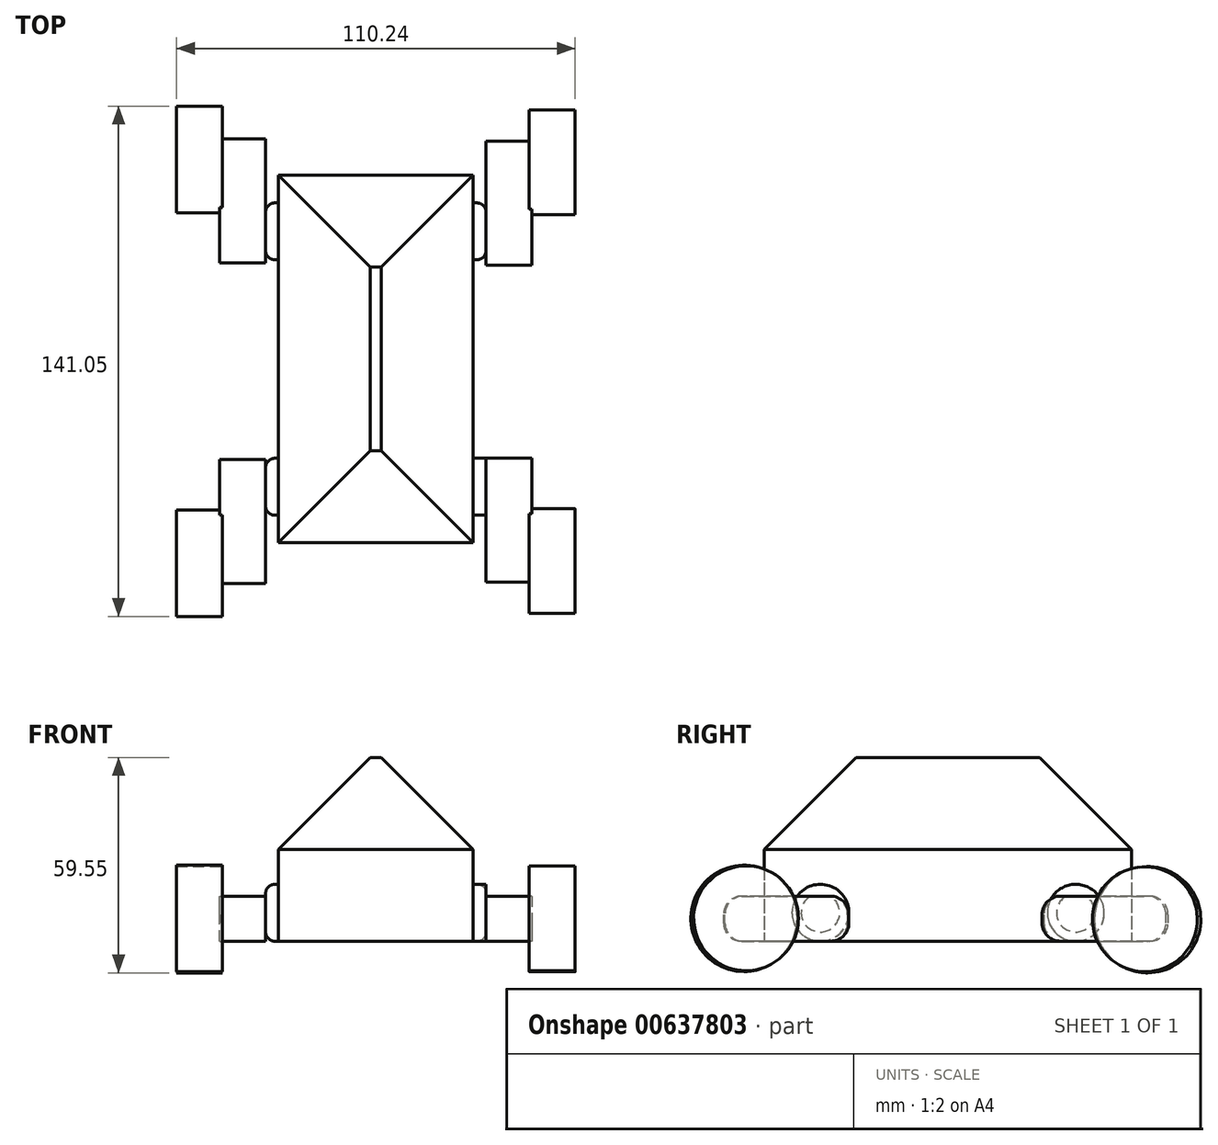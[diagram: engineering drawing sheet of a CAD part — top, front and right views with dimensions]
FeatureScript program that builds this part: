
annotation { "Feature Type Name" : "Feature", "Feature Type Description" : "" }
export const myFeature = defineFeature(function(context is Context, id is Id, definition is map)
    precondition{}
    {
        {
            var Q0;
            Q0=qCreatedBy(makeId("Top.planeOp"),FACE);
            var sketch = newSketch(context, id + "F0", { "sketchPlane" : qUnion([Q0])});
            skLineSegment(sketch, "E0.bottom", {"start": v(26.9, -50.8) * mm, "end": v(-26.9, -50.8) * mm});
            skLineSegment(sketch, "E0.top", {"start": v(26.9, 50.8) * mm, "end": v(-26.9, 50.8) * mm});
            skLineSegment(sketch, "E0.left", {"start": v(26.9, -50.8) * mm, "end": v(26.9, 50.8) * mm});
            skLineSegment(sketch, "E0.right", {"start": v(-26.9, -50.8) * mm, "end": v(-26.9, 50.8) * mm});
            skPoint(sketch, "E0.middle", {"position": v(0, 0) * mm});
            skSolve(sketch);
        }
        {
            var Q0;
            Q0=makeQuery(id+"F0.imprint","IMPRINT",FACE,{"disambiguationData":[TD([[makeQuery(id+"F0.imprint","IMPRINT",EDGE,{"derivedFrom":sQuery(id+"F0.wireOp",EDGE,"E0.bottom")}),-1.0]])]});
            extrude(context, id + "F1", {"entities" : qUnion([Q0]), "depth" : 25.4 * mm, "offsetDistance" : 25.4 * mm});
        }
        {
            var Q0;
            Q0=qCreatedBy(makeId("Right.planeOp"),FACE);
            var sketch = newSketch(context, id + "F2", { "sketchPlane" : qUnion([Q0])});
            skCircle(sketch, "E1", {"center": v(-35.31, 7.87) * mm, "radius": 7.87 * mm});
            skCircle(sketch, "E2", {"center": v(35.31, 7.87) * mm, "radius": 7.87 * mm});
            skSolve(sketch);
        }
        {
            var Q0;
            Q0 = qSketchRegion(id + "F2", true);
            extrude(context, id + "F3", {"entities" : qUnion([Q0]), "operationType" : NewBodyOperationType.ADD, "depth" : 30.48 * mm, "offsetDistance" : 25.4 * mm});
        }
        {
            var Q0;
            Q0=qCreatedBy(makeId("Right.planeOp"),FACE);
            var sketch = newSketch(context, id + "F4", { "sketchPlane" : qUnion([Q0])});
            skCircle(sketch, "E3", {"center": v(35.31, 7.87) * mm, "radius": 7.87 * mm});
            skCircle(sketch, "E4", {"center": v(-35.31, 7.87) * mm, "radius": 7.87 * mm});
            skSolve(sketch);
        }
        {
            var Q0;
            Q0 = qSketchRegion(id + "F4", true);
            extrude(context, id + "F5", {"entities" : qUnion([Q0]), "operationType" : NewBodyOperationType.ADD, "oppositeDirection" : true, "depth" : 30.48 * mm, "offsetDistance" : 25.4 * mm});
        }
        {
            var Q0;
            Q0=makeQuery(id+"F3.opExtrude","CAP_FACE",FACE,{"disambiguationData":[OSD([sQuery(id+"F2.wireOp",EDGE,"E1")])],"isStart":false});
            var Q1;
            Q1=makeQuery(id+"F3.opExtrude","CAP_FACE",FACE,{"disambiguationData":[OSD([sQuery(id+"F2.wireOp",EDGE,"E2")])],"isStart":false});
            var Q2;
            Q2=makeQuery(id+"F5.opExtrude","CAP_FACE",FACE,{"disambiguationData":[OSD([sQuery(id+"F4.wireOp",EDGE,"E3")])],"isStart":false});
            var Q3;
            Q3=makeQuery(id+"F5.opExtrude","CAP_FACE",FACE,{"disambiguationData":[OSD([sQuery(id+"F4.wireOp",EDGE,"E4")])],"isStart":false});
            fillet(context, id + "F6", {"entities" : qUnion([Q0, Q1, Q2, Q3]), "radius" : 2.54 * mm, "allowEdgeOverflow" : false});
        }
        {
            var Q0;
            Q0=qCreatedBy(makeId("Top.planeOp"),FACE);
            var sketch = newSketch(context, id + "F7", { "sketchPlane" : qUnion([Q0])});
            skLineSegment(sketch, "E5.bottom", {"start": v(-30.48, -27.81) * mm, "end": v(-43.18, -27.81) * mm});
            skLineSegment(sketch, "E5.top", {"start": v(-30.48, -62.1) * mm, "end": v(-43.18, -62.1) * mm});
            skLineSegment(sketch, "E5.left", {"start": v(-30.48, -27.81) * mm, "end": v(-30.48, -62.1) * mm});
            skLineSegment(sketch, "E5.right", {"start": v(-43.18, -27.81) * mm, "end": v(-43.18, -62.1) * mm});
            skPoint(sketch, "E5.middle", {"position": v(-36.83, -44.96) * mm});
            skLineSegment(sketch, "E6.bottom", {"start": v(-30.48, 60.82) * mm, "end": v(-43.18, 60.82) * mm});
            skLineSegment(sketch, "E6.top", {"start": v(-30.48, 26.53) * mm, "end": v(-43.18, 26.53) * mm});
            skLineSegment(sketch, "E6.left", {"start": v(-30.48, 60.82) * mm, "end": v(-30.48, 26.53) * mm});
            skLineSegment(sketch, "E6.right", {"start": v(-43.18, 60.82) * mm, "end": v(-43.18, 26.53) * mm});
            skLineSegment(sketch, "E7.bottom", {"start": v(43.18, 60.28) * mm, "end": v(30.48, 60.28) * mm});
            skLineSegment(sketch, "E7.top", {"start": v(43.18, 25.99) * mm, "end": v(30.48, 25.99) * mm});
            skLineSegment(sketch, "E7.left", {"start": v(43.18, 60.28) * mm, "end": v(43.18, 25.99) * mm});
            skLineSegment(sketch, "E7.right", {"start": v(30.48, 60.28) * mm, "end": v(30.48, 25.99) * mm});
            skLineSegment(sketch, "E8.bottom", {"start": v(43.18, -27.44) * mm, "end": v(30.48, -27.44) * mm});
            skLineSegment(sketch, "E8.top", {"start": v(43.18, -61.73) * mm, "end": v(30.48, -61.73) * mm});
            skLineSegment(sketch, "E8.left", {"start": v(43.18, -27.44) * mm, "end": v(43.18, -61.73) * mm});
            skLineSegment(sketch, "E8.right", {"start": v(30.48, -27.44) * mm, "end": v(30.48, -61.73) * mm});
            skSolve(sketch);
        }
        {
            var Q0;
            Q0=makeQuery(id+"F7.imprint","IMPRINT",FACE,{"disambiguationData":[TD([[makeQuery(id+"F7.imprint","IMPRINT",EDGE,{"derivedFrom":sQuery(id+"F7.wireOp",EDGE,"E8.bottom")}),1.0]])]});
            var Q1;
            Q1=makeQuery(id+"F7.imprint","IMPRINT",FACE,{"disambiguationData":[TD([[makeQuery(id+"F7.imprint","IMPRINT",EDGE,{"derivedFrom":sQuery(id+"F7.wireOp",EDGE,"E7.bottom")}),1.0]])]});
            var Q2;
            Q2=makeQuery(id+"F7.imprint","IMPRINT",FACE,{"disambiguationData":[TD([[makeQuery(id+"F7.imprint","IMPRINT",EDGE,{"derivedFrom":sQuery(id+"F7.wireOp",EDGE,"E6.bottom")}),1.0]])]});
            var Q3;
            Q3=makeQuery(id+"F7.imprint","IMPRINT",FACE,{"disambiguationData":[TD([[makeQuery(id+"F7.imprint","IMPRINT",EDGE,{"derivedFrom":sQuery(id+"F7.wireOp",EDGE,"E5.bottom")}),1.0]])]});
            extrude(context, id + "F8", {"entities" : qUnion([Q0, Q1, Q2, Q3]), "operationType" : NewBodyOperationType.ADD, "depth" : 12.45 * mm, "offsetDistance" : 25.4 * mm});
        }
        {
            var Q0;
            Q0=makeQuery(id+"F8.opExtrude","CAP_EDGE",EDGE,{"disambiguationData":[OSD([sQuery(id+"F7.wireOp",EDGE,"E8.top")])],"isStart":false});
            var Q1;
            Q1=makeQuery(id+"F8.opExtrude","CAP_EDGE",EDGE,{"disambiguationData":[OSD([sQuery(id+"F7.wireOp",EDGE,"E8.top")])],"isStart":true});
            var Q2;
            Q2=makeQuery(id+"F8.opExtrude","CAP_EDGE",EDGE,{"disambiguationData":[OSD([sQuery(id+"F7.wireOp",EDGE,"E8.bottom")])],"isStart":false});
            var Q3;
            Q3=makeQuery(id+"F8.opExtrude","CAP_EDGE",EDGE,{"disambiguationData":[OSD([sQuery(id+"F7.wireOp",EDGE,"E8.bottom")])],"isStart":true});
            var Q4;
            Q4=makeQuery(id+"F8.opExtrude","CAP_EDGE",EDGE,{"disambiguationData":[OSD([sQuery(id+"F7.wireOp",EDGE,"E7.bottom")])],"isStart":true});
            var Q5;
            Q5=makeQuery(id+"F8.opExtrude","CAP_EDGE",EDGE,{"disambiguationData":[OSD([sQuery(id+"F7.wireOp",EDGE,"E7.bottom")])],"isStart":false});
            var Q6;
            Q6=makeQuery(id+"F8.opExtrude","CAP_EDGE",EDGE,{"disambiguationData":[OSD([sQuery(id+"F7.wireOp",EDGE,"E7.top")])],"isStart":true});
            var Q7;
            Q7=makeQuery(id+"F8.opExtrude","CAP_EDGE",EDGE,{"disambiguationData":[OSD([sQuery(id+"F7.wireOp",EDGE,"E7.top")])],"isStart":false});
            var Q8;
            Q8=makeQuery(id+"F8.opExtrude","CAP_EDGE",EDGE,{"disambiguationData":[OSD([sQuery(id+"F7.wireOp",EDGE,"E5.top")])],"isStart":false});
            var Q9;
            Q9=makeQuery(id+"F8.opExtrude","CAP_EDGE",EDGE,{"disambiguationData":[OSD([sQuery(id+"F7.wireOp",EDGE,"E5.top")])],"isStart":true});
            var Q10;
            Q10=makeQuery(id+"F8.opExtrude","CAP_EDGE",EDGE,{"disambiguationData":[OSD([sQuery(id+"F7.wireOp",EDGE,"E5.bottom")])],"isStart":false});
            var Q11;
            Q11=makeQuery(id+"F8.opExtrude","CAP_EDGE",EDGE,{"disambiguationData":[OSD([sQuery(id+"F7.wireOp",EDGE,"E6.bottom")])],"isStart":false});
            var Q12;
            Q12=makeQuery(id+"F8.opExtrude","CAP_EDGE",EDGE,{"disambiguationData":[OSD([sQuery(id+"F7.wireOp",EDGE,"E5.bottom")])],"isStart":true});
            var Q13;
            Q13=makeQuery(id+"F8.opExtrude","CAP_EDGE",EDGE,{"disambiguationData":[OSD([sQuery(id+"F7.wireOp",EDGE,"E6.bottom")])],"isStart":true});
            var Q14;
            Q14=makeQuery(id+"F8.opExtrude","CAP_EDGE",EDGE,{"disambiguationData":[OSD([sQuery(id+"F7.wireOp",EDGE,"E6.top")])],"isStart":true});
            var Q15;
            Q15=makeQuery(id+"F8.opExtrude","CAP_EDGE",EDGE,{"disambiguationData":[OSD([sQuery(id+"F7.wireOp",EDGE,"E6.top")])],"isStart":false});
            fillet(context, id + "F9", {"entities" : qUnion([Q0, Q1, Q2, Q3, Q4, Q5, Q6, Q7, Q8, Q9, Q10, Q11, Q12, Q13, Q14, Q15]), "radius" : 5.08 * mm, "tangentPropagation" : true, "allowEdgeOverflow" : false});
        }
        {
            var Q0;
            Q0=qCreatedBy(makeId("Right.planeOp"),FACE);
            cPlane(context, id + "F10", {"entities" : qUnion([Q0]), "cplaneType" : CPlaneType.OFFSET, "offset" : 42.42 * mm, "width" : 152.4 * mm, "height" : 152.4 * mm});
        }
        {
            var Q0;
            Q0=qCreatedBy(makeId("Right.planeOp"),FACE);
            cPlane(context, id + "F11", {"entities" : qUnion([Q0]), "cplaneType" : CPlaneType.OFFSET, "offset" : 42.42 * mm, "oppositeDirection" : true, "width" : 152.4 * mm, "height" : 152.4 * mm});
        }
        {
            var Q0;
            Q0=qCreatedBy(id+"F10.planeOp",FACE);
            var sketch = newSketch(context, id + "F12", { "sketchPlane" : qUnion([Q0])});
            skCircle(sketch, "E9", {"center": v(-55.87, 6.33) * mm, "radius": 14.5 * mm});
            skCircle(sketch, "E10", {"center": v(54.43, 6.06) * mm, "radius": 14.5 * mm});
            skSolve(sketch);
        }
        {
            var Q0;
            Q0=makeQuery(id+"F12.imprint","IMPRINT",FACE,{"disambiguationData":[TD([[makeQuery(id+"F12.imprint","IMPRINT",EDGE,{"derivedFrom":sQuery(id+"F12.wireOp",EDGE,"E9")}),1.0]])]});
            var Q1;
            Q1=makeQuery(id+"F12.imprint","IMPRINT",FACE,{"disambiguationData":[TD([[makeQuery(id+"F12.imprint","IMPRINT",EDGE,{"derivedFrom":sQuery(id+"F12.wireOp",EDGE,"E10")}),1.0]])]});
            extrude(context, id + "F13", {"entities" : qUnion([Q0, Q1]), "operationType" : NewBodyOperationType.ADD, "depth" : 12.7 * mm, "offsetDistance" : 25.4 * mm});
        }
        {
            var Q0;
            Q0=qCreatedBy(id+"F11.planeOp",FACE);
            var sketch = newSketch(context, id + "F14", { "sketchPlane" : qUnion([Q0])});
            skCircle(sketch, "E11", {"center": v(55.19, 5.95) * mm, "radius": 14.7 * mm});
            skCircle(sketch, "E12", {"center": v(-56.46, 6.3) * mm, "radius": 14.7 * mm});
            skSolve(sketch);
        }
        {
            var Q0;
            Q0=makeQuery(id+"F14.imprint","IMPRINT",FACE,{"disambiguationData":[TD([[makeQuery(id+"F14.imprint","IMPRINT",EDGE,{"derivedFrom":sQuery(id+"F14.wireOp",EDGE,"E11")}),1.0]])]});
            var Q1;
            Q1=makeQuery(id+"F14.imprint","IMPRINT",FACE,{"disambiguationData":[TD([[makeQuery(id+"F14.imprint","IMPRINT",EDGE,{"derivedFrom":sQuery(id+"F14.wireOp",EDGE,"E12")}),1.0]])]});
            extrude(context, id + "F15", {"entities" : qUnion([Q0, Q1]), "operationType" : NewBodyOperationType.ADD, "oppositeDirection" : true, "depth" : 12.7 * mm, "offsetDistance" : 25.4 * mm});
        }
        {
            var Q0;
            Q0=makeQuery(id+"F1.opExtrude","CAP_FACE",FACE,{"disambiguationData":[OSD([sQuery(id+"F0.wireOp",EDGE,"E0.bottom"),sQuery(id+"F0.wireOp",EDGE,"E0.top"),sQuery(id+"F0.wireOp",EDGE,"E0.left"),sQuery(id+"F0.wireOp",EDGE,"E0.right")])],"isStart":false});
            cPlane(context, id + "F16", {"entities" : qUnion([Q0]), "cplaneType" : CPlaneType.OFFSET, "offset" : 0 * mm, "width" : 152.4 * mm, "height" : 152.4 * mm});
        }
        {
            var Q0;
            Q0=qCreatedBy(id+"F16.planeOp",FACE);
            var sketch = newSketch(context, id + "F17", { "sketchPlane" : qUnion([Q0])});
            skLineSegment(sketch, "E13.bottom", {"start": v(26.9, -50.8) * mm, "end": v(-26.9, -50.8) * mm});
            skLineSegment(sketch, "E13.top", {"start": v(26.9, 50.8) * mm, "end": v(-26.9, 50.8) * mm});
            skLineSegment(sketch, "E13.left", {"start": v(26.9, -50.8) * mm, "end": v(26.9, 50.8) * mm});
            skLineSegment(sketch, "E13.right", {"start": v(-26.9, -50.8) * mm, "end": v(-26.9, 50.8) * mm});
            skPoint(sketch, "E13.middle", {"position": v(0, 0) * mm});
            skSolve(sketch);
        }
        {
            var Q0;
            Q0 = qSketchRegion(id + "F17", true);
            extrude(context, id + "F18", {"entities" : qUnion([Q0]), "operationType" : NewBodyOperationType.ADD, "depth" : 25.4 * mm, "offsetDistance" : 25.4 * mm});
        }
        {
            var Q0;
            Q0=makeQuery(id+"F18.opExtrude","CAP_EDGE",EDGE,{"disambiguationData":[OSD([sQuery(id+"F17.wireOp",EDGE,"E13.top")])],"isStart":false});
            var Q1;
            Q1=makeQuery(id+"F18.opExtrude","CAP_EDGE",EDGE,{"disambiguationData":[OSD([sQuery(id+"F17.wireOp",EDGE,"E13.bottom")])],"isStart":false});
            chamfer(context, id + "F19", {"entities" : qUnion([Q0, Q1]), "width" : 25.4 * mm, "tangentPropagation" : true});
        }
        {
            var Q0;
            Q0=makeQuery(id+"F18.opExtrude","CAP_EDGE",EDGE,{"disambiguationData":[OSD([sQuery(id+"F17.wireOp",EDGE,"E13.right")])],"isStart":false});
            var Q1;
            Q1=makeQuery(id+"F18.opExtrude","CAP_EDGE",EDGE,{"disambiguationData":[OSD([sQuery(id+"F17.wireOp",EDGE,"E13.left")])],"isStart":false});
            chamfer(context, id + "F20", {"entities" : qUnion([Q0, Q1]), "width" : 25.4 * mm, "tangentPropagation" : true});
        }
    });
